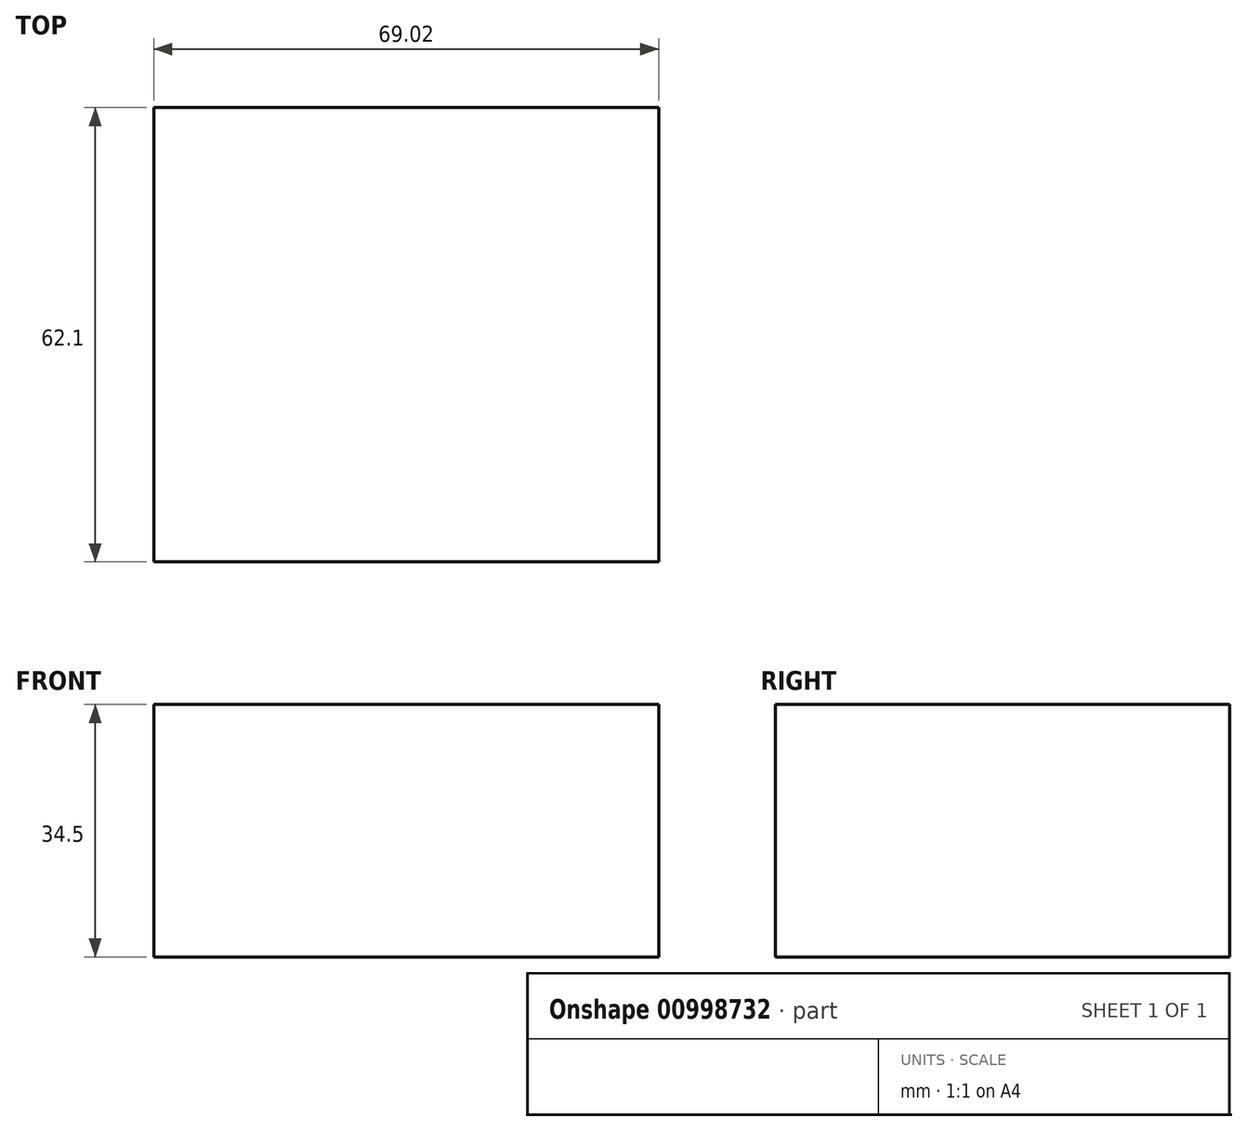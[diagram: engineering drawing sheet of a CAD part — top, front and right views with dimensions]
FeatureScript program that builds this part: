
annotation { "Feature Type Name" : "Feature", "Feature Type Description" : "" }
export const myFeature = defineFeature(function(context is Context, id is Id, definition is map)
    precondition{}
    {
        {
            var Q0;
            Q0=qCreatedBy(makeId("Top.planeOp"),FACE);
            var sketch = newSketch(context, id + "F0", { "sketchPlane" : qUnion([Q0])});
            skLineSegment(sketch, "E0.bottom", {"start": v(0, 0) * mm, "end": v(-69.02, 0) * mm});
            skLineSegment(sketch, "E0.top", {"start": v(0, -62.1) * mm, "end": v(-69.02, -62.1) * mm});
            skLineSegment(sketch, "E0.left", {"start": v(0, 0) * mm, "end": v(0, -62.1) * mm});
            skLineSegment(sketch, "E0.right", {"start": v(-69.02, 0) * mm, "end": v(-69.02, -62.1) * mm});
            skSolve(sketch);
        }
        {
            var Q0;
            Q0=makeQuery(id+"F0.imprint","IMPRINT",FACE,{"disambiguationData":[TD([[makeQuery(id+"F0.imprint","IMPRINT",EDGE,{"derivedFrom":sQuery(id+"F0.wireOp",EDGE,"E0.bottom")}),1.0]])]});
            var Q1;
            Q1=sQuery(id+"F0.wireOp",EDGE,"E0.right");
            extrude(context, id + "F1", {"entities" : qUnion([Q0]), "surfaceEntities" : qUnion([Q1]), "depth" : 34.5 * mm, "offsetDistance" : 25 * mm});
        }
    });
